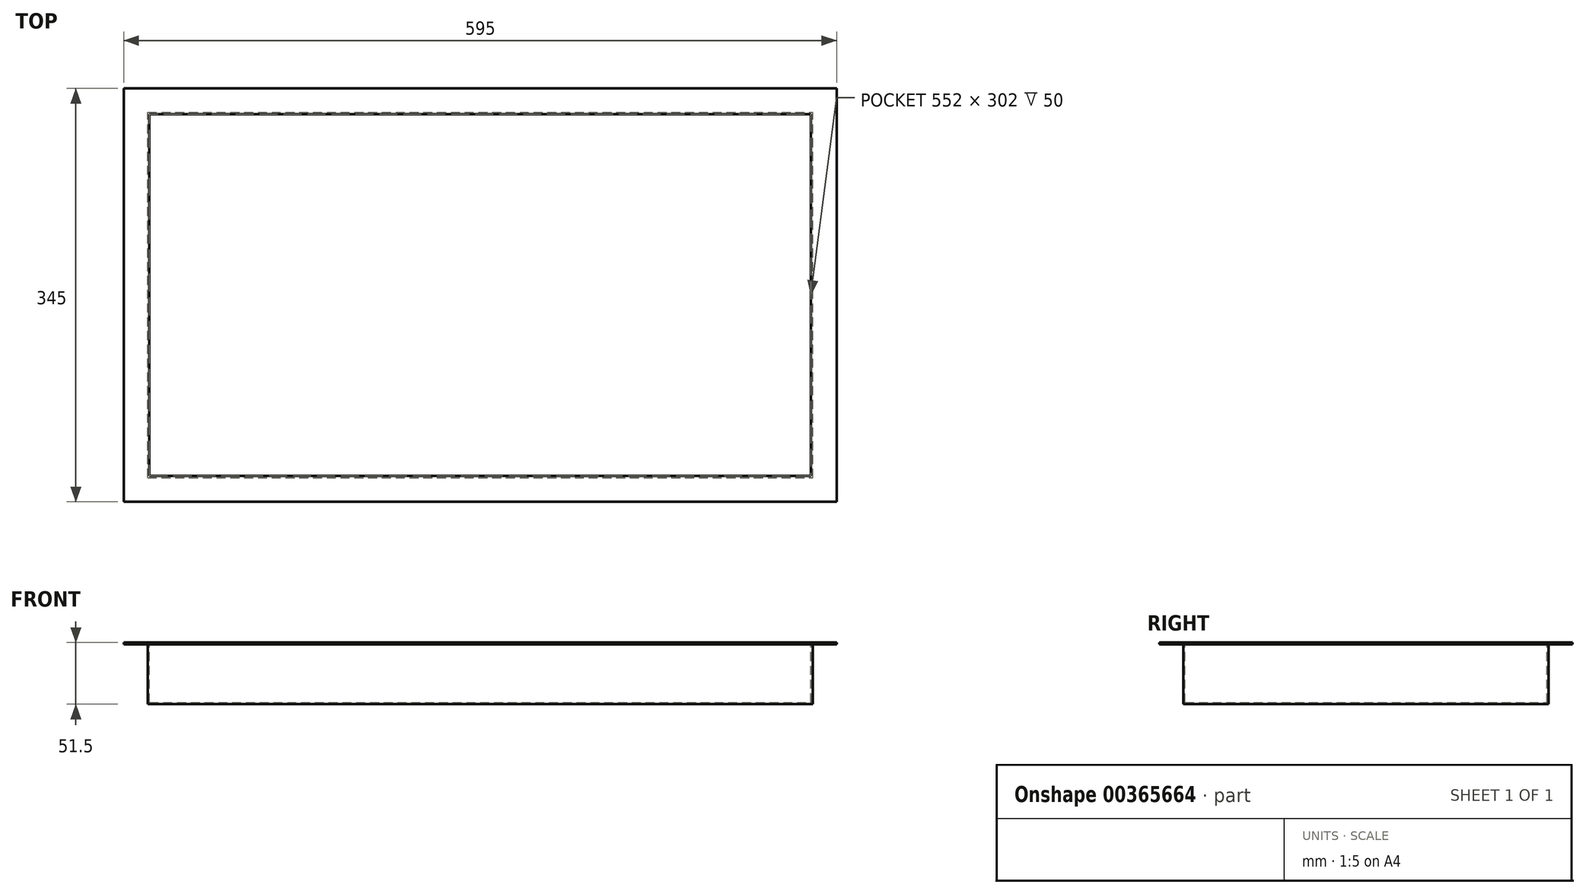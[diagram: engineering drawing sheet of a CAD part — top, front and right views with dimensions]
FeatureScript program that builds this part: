
annotation { "Feature Type Name" : "Feature", "Feature Type Description" : "" }
export const myFeature = defineFeature(function(context is Context, id is Id, definition is map)
    precondition{}
    {
        {
            var Q0;
            Q0=qCreatedBy(makeId("Top.planeOp"),FACE);
            var sketch = newSketch(context, id + "F0", { "sketchPlane" : qUnion([Q0])});
            skLineSegment(sketch, "E0.bottom", {"start": v(-277.5, -152.5) * mm, "end": v(277.5, -152.5) * mm});
            skLineSegment(sketch, "E0.top", {"start": v(-277.5, 152.5) * mm, "end": v(277.5, 152.5) * mm});
            skLineSegment(sketch, "E0.left", {"start": v(-277.5, -152.5) * mm, "end": v(-277.5, 152.5) * mm});
            skLineSegment(sketch, "E0.right", {"start": v(277.5, -152.5) * mm, "end": v(277.5, 152.5) * mm});
            skPoint(sketch, "E0.middle", {"position": v(0, 0) * mm});
            skSolve(sketch);
        }
        {
            var Q0;
            Q0=makeQuery(id+"F0.imprint","IMPRINT",FACE,{"disambiguationData":[TD([[makeQuery(id+"F0.imprint","IMPRINT",EDGE,{"derivedFrom":sQuery(id+"F0.wireOp",EDGE,"E0.bottom")}),1.0]])]});
            extrude(context, id + "F1", {"entities" : qUnion([Q0]), "oppositeDirection" : true, "depth" : 50 * mm});
        }
        {
            var Q0;
            Q0=makeQuery(id+"F1.opExtrude","CAP_FACE",FACE,{"disambiguationData":[OSD([sQuery(id+"F0.wireOp",EDGE,"E0.bottom"),sQuery(id+"F0.wireOp",EDGE,"E0.top"),sQuery(id+"F0.wireOp",EDGE,"E0.left"),sQuery(id+"F0.wireOp",EDGE,"E0.right")])],"isStart":true});
            var sketch = newSketch(context, id + "F2", { "sketchPlane" : qUnion([Q0])});
            skLineSegment(sketch, "E1.bottom", {"start": v(-297.5, -172.5) * mm, "end": v(297.5, -172.5) * mm});
            skLineSegment(sketch, "E1.top", {"start": v(-297.5, 172.5) * mm, "end": v(297.5, 172.5) * mm});
            skLineSegment(sketch, "E1.left", {"start": v(-297.5, -172.5) * mm, "end": v(-297.5, 172.5) * mm});
            skLineSegment(sketch, "E1.right", {"start": v(297.5, -172.5) * mm, "end": v(297.5, 172.5) * mm});
            skPoint(sketch, "E1.middle", {"position": v(0, 0) * mm});
            skSolve(sketch);
        }
        {
            var Q0;
            Q0=makeQuery(id+"F2.imprint","IMPRINT",FACE,{"disambiguationData":[TD([[makeQuery(id+"F2.imprint","IMPRINT",EDGE,{"derivedFrom":sQuery(id+"F2.wireOp",EDGE,"E1.bottom")}),1.0]])]});
            var Q1;
            Q1=makeQuery(id+"F2.imprint","IMPRINT",FACE,{"disambiguationData":[TD([[makeQuery(id+"F2.imprint","IMPRINT",EDGE,{"derivedFrom":makeQuery(id+"F1.opExtrude","CAP_EDGE",EDGE,{"disambiguationData":[OSD([sQuery(id+"F0.wireOp",EDGE,"E0.bottom")])],"isStart":true})}),1.0]])]});
            extrude(context, id + "F3", {"entities" : qUnion([Q0, Q1]), "operationType" : NewBodyOperationType.ADD, "depth" : 1.5 * mm});
        }
        {
            var Q0;
            Q0=makeQuery(id+"F3.opExtrude","CAP_FACE",FACE,{"disambiguationData":[OSD([sQuery(id+"F2.wireOp",EDGE,"E1.bottom"),sQuery(id+"F2.wireOp",EDGE,"E1.top"),sQuery(id+"F2.wireOp",EDGE,"E1.left"),sQuery(id+"F2.wireOp",EDGE,"E1.right")])],"isStart":false});
            shell(context, id + "F4", {"entities" : qUnion([Q0]), "thickness" : 1.5 * mm});
        }
    });
